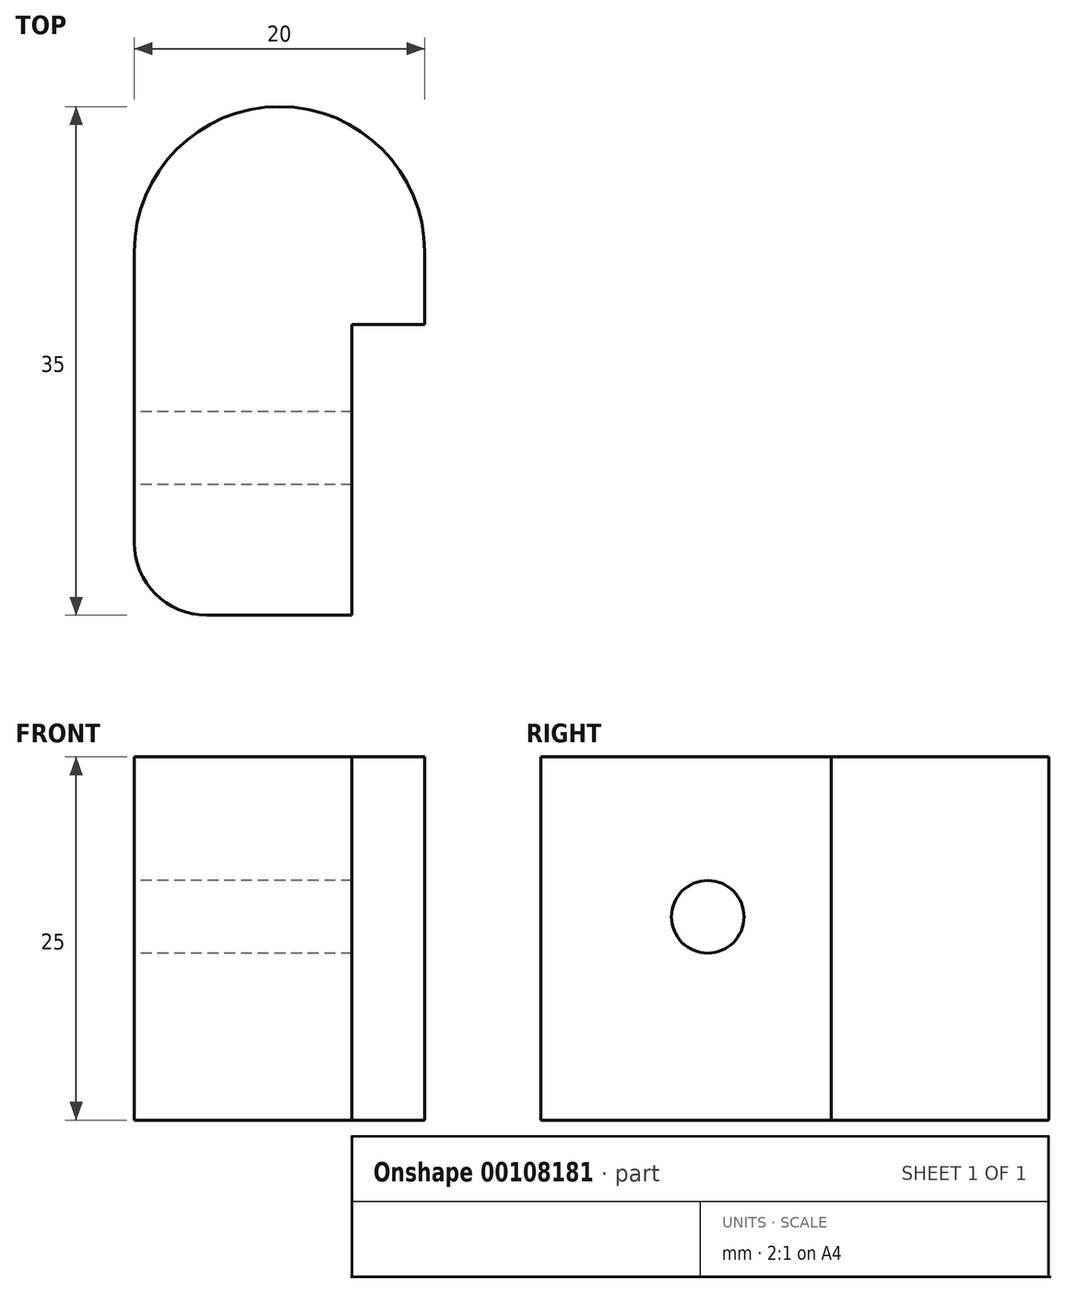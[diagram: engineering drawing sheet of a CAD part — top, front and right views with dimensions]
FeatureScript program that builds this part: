
annotation { "Feature Type Name" : "Feature", "Feature Type Description" : "" }
export const myFeature = defineFeature(function(context is Context, id is Id, definition is map)
    precondition{}
    {
        {
            var Q0;
            Q0=qCreatedBy(makeId("Top.planeOp"),FACE);
            var sketch = newSketch(context, id + "F0", { "sketchPlane" : qUnion([Q0])});
            skArc(sketch, "E0", {"start": v(10, 0) * mm, "mid": v(0, 10) * mm, "end": v(-10, 0) * mm});
            skLineSegment(sketch, "E1", {"start": v(-10, 0) * mm, "end": v(-10, -25) * mm});
            skLineSegment(sketch, "E2", {"start": v(-10, -25) * mm, "end": v(5, -25) * mm});
            skLineSegment(sketch, "E3", {"start": v(5, -25) * mm, "end": v(5, -5) * mm});
            skLineSegment(sketch, "E4", {"start": v(5, -5) * mm, "end": v(10, -5) * mm});
            skLineSegment(sketch, "E5", {"start": v(10, -5) * mm, "end": v(10, 0) * mm});
            skSolve(sketch);
        }
        {
            var Q0;
            Q0=makeQuery(id+"F0.imprint","IMPRINT",FACE,{"disambiguationData":[TD([[makeQuery(id+"F0.imprint","IMPRINT",EDGE,{"derivedFrom":sQuery(id+"F0.wireOp",EDGE,"E0")}),1.0]])]});
            extrude(context, id + "F1", {"entities" : qUnion([Q0]), "depth" : 25 * mm});
        }
        {
            var Q0;
            Q0=makeQuery(id+"F1.opExtrude","SWEPT_FACE",FACE,{"disambiguationData":[OSD([sQuery(id+"F0.wireOp",EDGE,"E1")])]});
            var sketch = newSketch(context, id + "F2", { "sketchPlane" : qUnion([Q0])});
            skCircle(sketch, "E6", {"center": v(13.5, 14) * mm, "radius": 4.66 * mm});
            skSolve(sketch);
        }
        {
            var Q0;
            Q0=sQuery(id+"F2.wireOp",VERTEX,"E6.center");
            var Q1;
            Q1=makeQuery(id+"F1.opExtrude","SWEPT_BODY",BODY,{"disambiguationData":[OSD([sQuery(id+"F0.wireOp",EDGE,"E0"),sQuery(id+"F0.wireOp",EDGE,"E1"),sQuery(id+"F0.wireOp",EDGE,"E2"),sQuery(id+"F0.wireOp",EDGE,"E3"),sQuery(id+"F0.wireOp",EDGE,"E4"),sQuery(id+"F0.wireOp",EDGE,"E5")])]});
            hole(context, id + "F3", {"style" : HoleStyle.SIMPLE, "endStyle" : HoleEndStyle.THROUGH, "holeDiameter" : 5 * mm, "locations" : qUnion([Q0]), "scope" : qUnion([Q1]), "isTappedThrough" : true});
        }
        {
            var Q0;
            Q0=makeQuery(id+"F1.opExtrude","SWEPT_EDGE",EDGE,{"disambiguationData":[OSD([sQuery(id+"F0.wireOp",EDGE,"E1"),sQuery(id+"F0.wireOp",EDGE,"E2")])]});
            fillet(context, id + "F4", {"entities" : qUnion([Q0]), "radius" : 5 * mm, "tangentPropagation" : true, "allowEdgeOverflow" : false});
        }
    });
